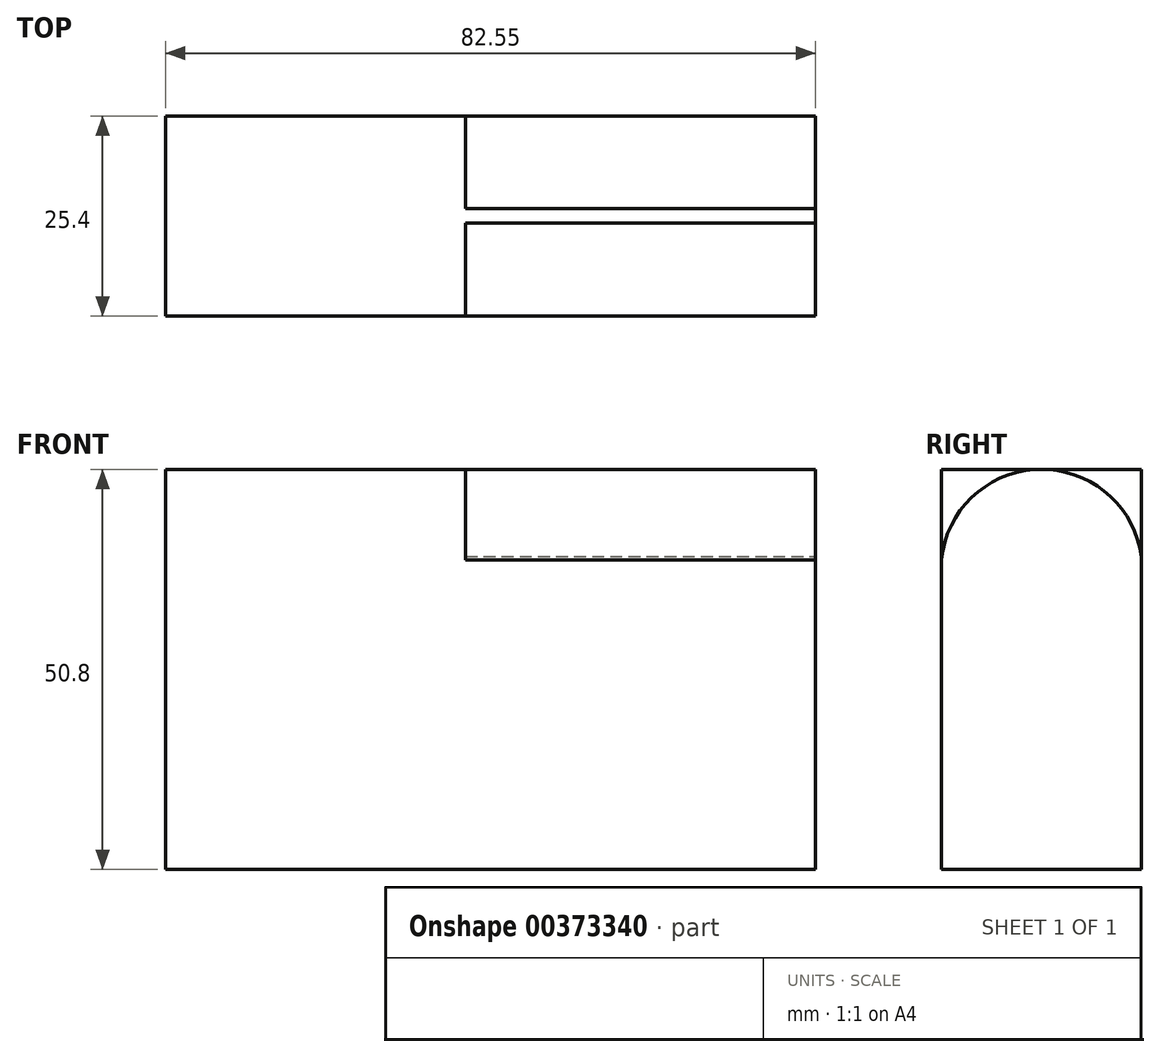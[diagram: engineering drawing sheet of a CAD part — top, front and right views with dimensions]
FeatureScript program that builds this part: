
annotation { "Feature Type Name" : "Feature", "Feature Type Description" : "" }
export const myFeature = defineFeature(function(context is Context, id is Id, definition is map)
    precondition{}
    {
        {
            var Q0;
            Q0=qCreatedBy(makeId("Front.planeOp"),FACE);
            var sketch = newSketch(context, id + "F0", { "sketchPlane" : qUnion([Q0])});
            skLineSegment(sketch, "E0", {"start": v(0, 50.8) * mm, "end": v(0, 0) * mm});
            skLineSegment(sketch, "E1", {"start": v(0, 0) * mm, "end": v(82.55, 0) * mm});
            skLineSegment(sketch, "E2", {"start": v(82.55, 0) * mm, "end": v(82.55, 50.8) * mm});
            skLineSegment(sketch, "E3", {"start": v(82.55, 50.8) * mm, "end": v(0, 50.8) * mm});
            skSolve(sketch);
        }
        {
            var Q0;
            Q0=makeQuery(id+"F0.imprint","IMPRINT",FACE,{"disambiguationData":[TD([[makeQuery(id+"F0.imprint","IMPRINT",EDGE,{"derivedFrom":sQuery(id+"F0.wireOp",EDGE,"E0")}),1.0]])]});
            extrude(context, id + "F1", {"entities" : qUnion([Q0]), "depth" : 25.4 * mm});
        }
        {
            var Q0;
            Q0=makeQuery(id+"F1.opExtrude","SWEPT_FACE",FACE,{"disambiguationData":[OSD([sQuery(id+"F0.wireOp",EDGE,"E2")])]});
            var sketch = newSketch(context, id + "F2", { "sketchPlane" : qUnion([Q0])});
            skArc(sketch, "E4", {"start": v(0, 36.33) * mm, "mid": v(-12.47, 50.83) * mm, "end": v(-25.4, 36.74) * mm});
            skSolve(sketch);
        }
        {
            var Q0;
            {var subQ0=sQuery(id+"F2.wireOp",EDGE,"E4");var subQ1=sQuery(id+"F0.wireOp",EDGE,"E2");var subQ2=makeQuery(id+"F1.opExtrude","CAP_EDGE",EDGE,{"disambiguationData":[OSD([subQ1])],"isStart":true});var subQ3=makeQuery(id+"F2.imprint","INTERSECT",VERTEX,{"disambiguationData":[OD(1.0)],"derivedFrom":[subQ2,subQ0]});Q0=makeQuery(id+"F2.imprint","IMPRINT",FACE,{"disambiguationData":[TD([[makeQuery(id+"F2.imprint","IMPRINT",EDGE,{"disambiguationData":[TD([[subQ3,-1.0]])],"derivedFrom":subQ0}),-1.0]])]});}
            var Q1;
            {var subQ0=sQuery(id+"F2.wireOp",EDGE,"E4");var subQ1=sQuery(id+"F0.wireOp",EDGE,"E2");var subQ4=makeQuery(id+"F1.opExtrude","CAP_EDGE",EDGE,{"disambiguationData":[OSD([subQ1])],"isStart":false});var subQ5=makeQuery(id+"F2.imprint","INTERSECT",VERTEX,{"disambiguationData":[OD(1.0)],"derivedFrom":[subQ4,subQ0]});Q1=makeQuery(id+"F2.imprint","IMPRINT",FACE,{"disambiguationData":[TD([[makeQuery(id+"F2.imprint","IMPRINT",EDGE,{"disambiguationData":[TD([[subQ5,1.0]])],"derivedFrom":subQ0}),-1.0]])]});}
            extrude(context, id + "F3", {"entities" : qUnion([Q0, Q1]), "operationType" : NewBodyOperationType.REMOVE, "oppositeDirection" : true, "depth" : 44.45 * mm});
        }
    });
